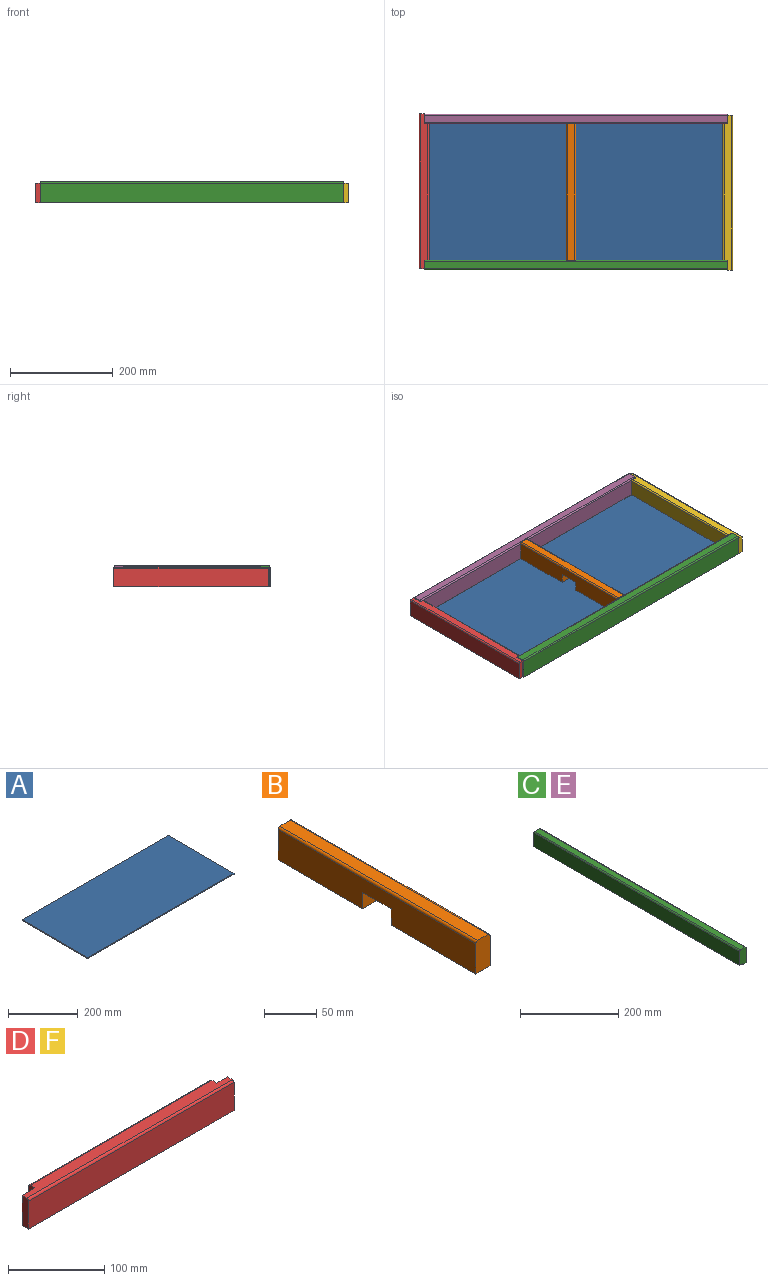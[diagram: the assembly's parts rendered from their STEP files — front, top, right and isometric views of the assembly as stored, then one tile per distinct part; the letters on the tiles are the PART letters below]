
ASSEMBLY  parts=6 mates=5
PART A: 6 faces, bbox 590.6x266.7x3.2 mm
  f0: plane 590.55x3.18mm, normal (0,-1,0), area 1875mm2, adj f1,f3,f4,f5
  f1: plane 266.7x3.18mm, normal (1,0,0), area 846.8mm2, adj f0,f2,f4,f5
  f2: plane 590.55x3.18mm, normal (0,1,0), area 1875mm2, adj f1,f3,f4,f5
  f3: plane 266.7x3.18mm, normal (-1,0,0), area 846.8mm2, adj f0,f2,f4,f5
  f4: plane 590.55x266.7mm, normal (0,0,1), area 157499.7mm2, adj f0,f1,f2,f3
  f5: plane 590.55x266.7mm, normal (0,0,-1), area 157499.7mm2, adj f0,f1,f2,f3
PART B: 12 faces, bbox 19.1x266.7x38.1 mm
  f0: plane 114.3x19.05mm, normal (0,0,-1), area 2177.4mm2, adj f1,f2,f3,f9
  f1: plane 266.7x35.56mm, normal (1,0,0), area 8758mm2, adj f0,f3,f4,f6,f7,f9,f10,f11
  f2: plane 266.7x35.56mm, normal (-1,0,0), area 8758mm2, adj f0,f3,f4,f6,f8,f9,f10,f11
  f3: plane 38.1x19.05mm, normal (0,-1,0), area 723mm2, adj f0,f1,f2,f5,f7,f8
  f4: plane 38.1x19.05mm, normal (0,1,0), area 723mm2, adj f1,f2,f5,f6,f7,f8
  f5: plane 266.7x13.97mm, normal (0,0,1), area 3725.8mm2, adj f3,f4,f7,f8
  f6: plane 114.3x19.05mm, normal (0,0,-1), area 2177.4mm2, adj f1,f2,f4,f10
  f7: cylinder r=2.54mm len=266.7mm, axis (0,-1,0), area 1064.1mm2, adj f1,f3,f4,f5
  f8: cylinder r=2.54mm len=266.7mm, axis (0,1,0), area 1064.1mm2, adj f2,f3,f4,f5
  f9: plane 19.05x19.05mm, normal (0,1,0), area 362.9mm2, adj f0,f1,f2,f11
  f10: plane 19.05x19.05mm, normal (0,-1,0), area 362.9mm2, adj f1,f2,f6,f11
  f11: plane 38.1x19.05mm, normal (0,0,-1), area 725.8mm2, adj f1,f2,f9,f10
PART C: 10 faces, bbox 19.1x590.6x40.6 mm
  f0: plane 590.55x38.1mm, normal (1,0,0), area 22500mm2, adj f1,f7,f8,f9
  f1: cylinder r=2.54mm len=590.55mm, axis (0,1,0), area 2356.2mm2, adj f0,f2,f8,f9
  f2: plane 590.55x13.97mm, normal (0,0,1), area 8250mm2, adj f1,f3,f8,f9
  f3: cylinder r=2.54mm len=590.55mm, axis (0,1,0), area 2356.2mm2, adj f2,f4,f8,f9
  f4: plane 590.55x34.93mm, normal (-1,0,0), area 20625mm2, adj f3,f5,f8,f9
  f5: plane 590.55x9.53mm, normal (0,0,-1), area 5625mm2, adj f4,f6,f8,f9
  f6: plane 590.55x3.18mm, normal (-1,0,0), area 1875mm2, adj f5,f7,f8,f9
  f7: plane 590.55x9.53mm, normal (0,0,-1), area 5625mm2, adj f0,f6,f8,f9
  f8: plane 40.64x19.05mm, normal (0,-1,0), area 741.2mm2, adj f0,f1,f2,f3,f4,f5,f6,f7
  f9: plane 40.64x19.05mm, normal (0,1,0), area 741.2mm2, adj f0,f1,f2,f3,f4,f5,f6,f7
PART D: 12 faces, bbox 301.6x19.1x38.1 mm
  f0: plane 34.93x9.53mm, normal (-1,0,0), area 331.3mm2, adj f4,f6,f7,f10,f11
  f1: plane 38.1x9.53mm, normal (-1,0,0), area 361.5mm2, adj f2,f4,f7,f8,f9
  f2: plane 301.63x35.56mm, normal (0,-1,0), area 10725.8mm2, adj f1,f3,f8,f9
  f3: plane 38.1x9.53mm, normal (1,0,0), area 361.5mm2, adj f2,f4,f7,f8,f9
  f4: plane 301.63x38.1mm, normal (0,1,0), area 2177.4mm2, adj f0,f1,f3,f5,f7,f8,f11
  f5: plane 34.93x9.53mm, normal (1,0,0), area 331.3mm2, adj f4,f6,f7,f10,f11
  f6: plane 266.7x32.39mm, normal (0,1,0), area 8637.1mm2, adj f0,f5,f10,f11
  f7: plane 301.63x13.97mm, normal (0,0,1), area 3969.8mm2, adj f0,f1,f3,f4,f5,f9,f10
  f8: plane 301.63x9.53mm, normal (0,0,-1), area 2873mm2, adj f1,f2,f3,f4
  f9: cylinder r=2.54mm len=301.63mm, axis (-1,0,0), area 1203.4mm2, adj f1,f2,f3,f7
  f10: cylinder r=2.54mm len=266.7mm, axis (1,0,0), area 1064.1mm2, adj f0,f5,f6,f7
  f11: plane 266.7x9.53mm, normal (0,0,-1), area 2540.3mm2, adj f0,f4,f5,f6
PART E: same geometry as C
PART F: same geometry as D
PLACE A t=(-25.02,80.93,9.9)mm fixed
PLACE B t=(-34.55,80.93,13.07)mm
PLACE C rot(axis=(0,0,-1),90deg) t=(270.25,-61.31,30.22)mm
PLACE D rot(axis=(0,0,-1),90deg) t=(-320.3,214.28,9.9)mm
PLACE E rot(axis=(0,0,1),90deg) t=(-320.3,223.17,30.22)mm
PLACE F rot(axis=(0,0,1),90deg) t=(270.25,-52.42,9.9)mm
MATE fastened D.f4 <-> C.f1  axis (1,0,0) through (-320.3,-68.3,48)mm
MATE fastened B.f0 <-> A.f4  axis (0,0,1) through (-25.02,-52.42,13.07)mm
MATE fastened D.f11 <-> A.f4  axis (0,0,-1) through (-320.3,80.93,13.07)mm
MATE fastened E.f1 <-> F.f4  axis (1,0,0) through (270.25,230.15,48)mm
MATE fastened F.f11 <-> A.f4  axis (0,0,-1) through (270.25,80.93,13.07)mm
